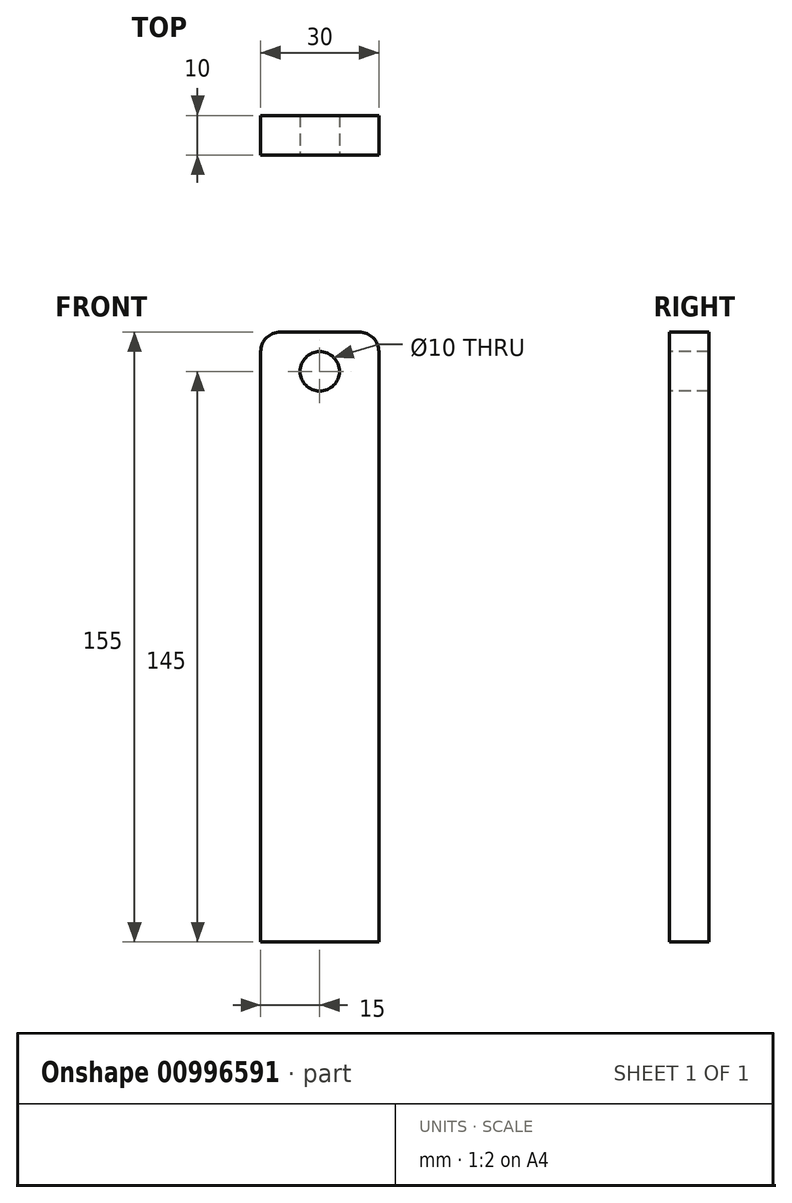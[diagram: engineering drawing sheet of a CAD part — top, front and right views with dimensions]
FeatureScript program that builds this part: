
annotation { "Feature Type Name" : "Feature", "Feature Type Description" : "" }
export const myFeature = defineFeature(function(context is Context, id is Id, definition is map)
    precondition{}
    {
        {
            var Q0;
            Q0=qCreatedBy(makeId("Front.planeOp"),FACE);
            var sketch = newSketch(context, id + "F0", { "sketchPlane" : qUnion([Q0])});
            skLineSegment(sketch, "E0.bottom", {"start": v(-15, 77.5) * mm, "end": v(15, 77.5) * mm});
            skLineSegment(sketch, "E0.top", {"start": v(-15, -77.5) * mm, "end": v(15, -77.5) * mm});
            skLineSegment(sketch, "E0.left", {"start": v(-15, 77.5) * mm, "end": v(-15, -77.5) * mm});
            skLineSegment(sketch, "E0.right", {"start": v(15, 77.5) * mm, "end": v(15, -77.5) * mm});
            skSolve(sketch);
        }
        {
            var Q0;
            Q0=makeQuery(id+"F0.imprint","IMPRINT",FACE,{"disambiguationData":[TD([[makeQuery(id+"F0.imprint","IMPRINT",EDGE,{"derivedFrom":sQuery(id+"F0.wireOp",EDGE,"E0.bottom")}),-1.0]])]});
            var Q1;
            Q1 = qSketchRegion(id + "F2", true);
            extrude(context, id + "F1", {"entities" : qUnion([Q0, Q1]), "depth" : 10 * mm, "offsetDistance" : 25 * mm});
        }
        {
            var Q0;
            Q0=makeQuery(id+"F1.opExtrude","CAP_FACE",FACE,{"disambiguationData":[OSD([sQuery(id+"F0.wireOp",EDGE,"E0.bottom"),sQuery(id+"F0.wireOp",EDGE,"E0.top"),sQuery(id+"F0.wireOp",EDGE,"E0.left"),sQuery(id+"F0.wireOp",EDGE,"E0.right")])],"isStart":false});
            var sketch = newSketch(context, id + "F2", { "sketchPlane" : qUnion([Q0])});
            skCircle(sketch, "E1", {"center": v(0, 67.5) * mm, "radius": 5 * mm});
            skSolve(sketch);
        }
        {
            var Q0;
            Q0=makeQuery(id+"F2.imprint","IMPRINT",FACE,{"disambiguationData":[TD([[makeQuery(id+"F2.imprint","IMPRINT",EDGE,{"derivedFrom":sQuery(id+"F2.wireOp",EDGE,"E1")}),1.0]])]});
            extrude(context, id + "F3", {"entities" : qUnion([Q0]), "operationType" : NewBodyOperationType.REMOVE, "endBound" : BoundingType.THROUGH_ALL, "oppositeDirection" : true, "depth" : 25 * mm, "offsetDistance" : 25 * mm});
        }
        {
            var Q0;
            Q0=makeQuery(id+"F1.opExtrude","SWEPT_EDGE",EDGE,{"disambiguationData":[OSD([sQuery(id+"F0.wireOp",EDGE,"E0.bottom"),sQuery(id+"F0.wireOp",EDGE,"E0.right")])]});
            var Q1;
            Q1=makeQuery(id+"F1.opExtrude","SWEPT_EDGE",EDGE,{"disambiguationData":[OSD([sQuery(id+"F0.wireOp",EDGE,"E0.bottom"),sQuery(id+"F0.wireOp",EDGE,"E0.left")])]});
            fillet(context, id + "F4", {"entities" : qUnion([Q0, Q1]), "radius" : 5 * mm, "tangentPropagation" : true, "allowEdgeOverflow" : false});
        }
    });
